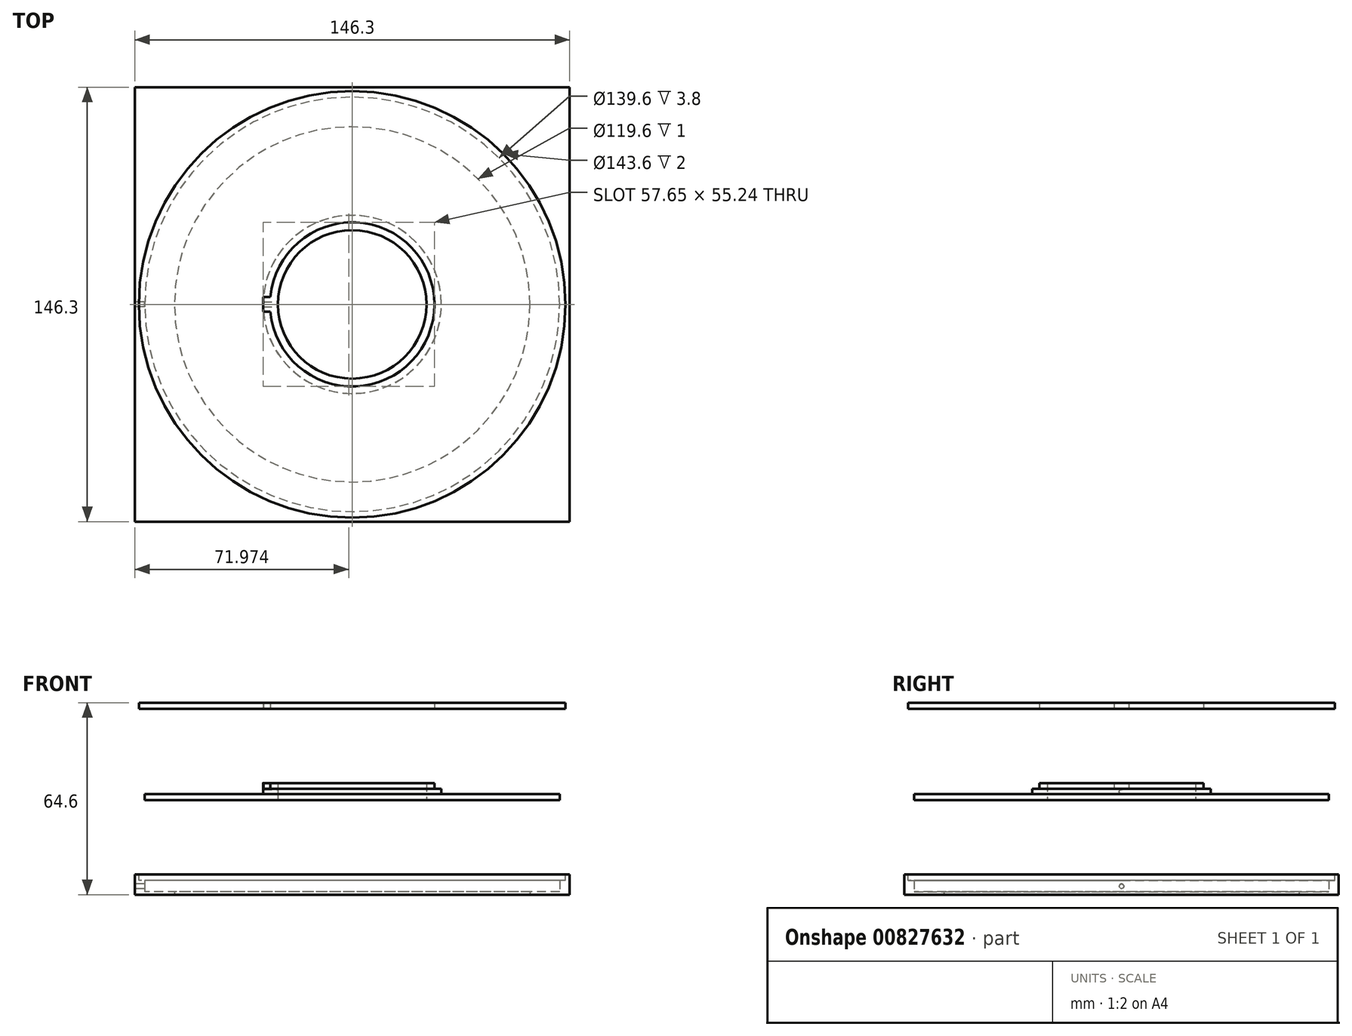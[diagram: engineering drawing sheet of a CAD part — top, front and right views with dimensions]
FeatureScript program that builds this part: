
annotation { "Feature Type Name" : "Feature", "Feature Type Description" : "" }
export const myFeature = defineFeature(function(context is Context, id is Id, definition is map)
    precondition{}
    {
        {
            var Q0;
            Q0=qCreatedBy(makeId("Top.planeOp"),FACE);
            var sketch = newSketch(context, id + "F0", { "sketchPlane" : qUnion([Q0])});
            skLineSegment(sketch, "E0.bottom", {"start": v(-73.15, 73.15) * mm, "end": v(73.15, 73.15) * mm});
            skLineSegment(sketch, "E0.top", {"start": v(-73.15, -73.15) * mm, "end": v(73.15, -73.15) * mm});
            skLineSegment(sketch, "E0.left", {"start": v(-73.15, 73.15) * mm, "end": v(-73.15, -73.15) * mm});
            skLineSegment(sketch, "E0.right", {"start": v(73.15, 73.15) * mm, "end": v(73.15, -73.15) * mm});
            skLineSegment(sketch, "E1", {"start": v(0, 73.15) * mm, "end": v(0, -73.15) * mm, "construction": true});
            skLineSegment(sketch, "E2", {"start": v(-73.15, 0) * mm, "end": v(73.15, 0) * mm, "construction": true});
            skCircle(sketch, "E3", {"center": v(0, 0) * mm, "radius": 59.8 * mm});
            skCircle(sketch, "E4", {"center": v(0, 0) * mm, "radius": 69.8 * mm});
            skCircle(sketch, "E5", {"center": v(0, 0) * mm, "radius": 25 * mm, "construction": true});
            skCircle(sketch, "E6", {"center": v(0, 0) * mm, "radius": 30 * mm, "construction": true});
            skSolve(sketch);
        }
        {
            var Q0;
            Q0=makeQuery(id+"F0.imprint","IMPRINT",FACE,{"disambiguationData":[TD([[makeQuery(id+"F0.imprint","IMPRINT",EDGE,{"derivedFrom":sQuery(id+"F0.wireOp",EDGE,"E0.bottom")}),-1.0]])]});
            extrude(context, id + "F1", {"entities" : qUnion([Q0]), "depth" : 6.8 * mm, "offsetDistance" : 25 * mm});
        }
        {
            var Q0;
            Q0=makeQuery(id+"F0.imprint","IMPRINT",FACE,{"disambiguationData":[TD([[makeQuery(id+"F0.imprint","IMPRINT",EDGE,{"derivedFrom":sQuery(id+"F0.wireOp",EDGE,"E3")}),-1.0]])]});
            extrude(context, id + "F2", {"entities" : qUnion([Q0]), "operationType" : NewBodyOperationType.ADD, "depth" : 1 * mm, "offsetDistance" : 25 * mm});
        }
        {
            var Q0;
            Q0=makeQuery(id+"F1.opExtrude","CAP_FACE",FACE,{"disambiguationData":[OSD([sQuery(id+"F0.wireOp",EDGE,"E0.bottom"),sQuery(id+"F0.wireOp",EDGE,"E0.top"),sQuery(id+"F0.wireOp",EDGE,"E0.left"),sQuery(id+"F0.wireOp",EDGE,"E0.right"),sQuery(id+"F0.wireOp",EDGE,"E4")])],"isStart":false});
            cPlane(context, id + "F3", {"entities" : qUnion([Q0]), "cplaneType" : CPlaneType.OFFSET, "offset" : 25 * mm, "width" : 150 * mm, "height" : 150 * mm});
        }
        {
            var Q0;
            Q0=qCreatedBy(id+"F3.planeOp",FACE);
            var sketch = newSketch(context, id + "F4", { "sketchPlane" : qUnion([Q0])});
            skCircle(sketch, "E7.0", {"center": v(0, 0) * mm, "radius": 25 * mm});
            skCircle(sketch, "E7.1", {"center": v(0, 0) * mm, "radius": 30 * mm});
            skCircle(sketch, "E7.2", {"center": v(0, 0) * mm, "radius": 69.8 * mm});
            skSolve(sketch);
        }
        {
            var Q0;
            Q0=makeQuery(id+"F4.imprint","IMPRINT",FACE,{"disambiguationData":[TD([[makeQuery(id+"F4.imprint","IMPRINT",EDGE,{"derivedFrom":sQuery(id+"F4.wireOp",EDGE,"E7.1")}),-1.0]])]});
            extrude(context, id + "F5", {"entities" : qUnion([Q0]), "depth" : 2 * mm, "offsetDistance" : 25 * mm});
        }
        {
            var Q0;
            Q0=makeQuery(id+"F4.imprint","IMPRINT",FACE,{"disambiguationData":[TD([[makeQuery(id+"F4.imprint","IMPRINT",EDGE,{"derivedFrom":sQuery(id+"F4.wireOp",EDGE,"E7.0")}),-1.0]])]});
            extrude(context, id + "F6", {"entities" : qUnion([Q0]), "operationType" : NewBodyOperationType.ADD, "depth" : 3.8 * mm, "offsetDistance" : 25 * mm});
        }
        {
            var Q0;
            Q0=makeQuery(id+"F6.opExtrude","CAP_FACE",FACE,{"disambiguationData":[OSD([sQuery(id+"F4.wireOp",EDGE,"E7.0"),sQuery(id+"F4.wireOp",EDGE,"E7.1")])],"isStart":false});
            var sketch = newSketch(context, id + "F7", { "sketchPlane" : qUnion([Q0])});
            skCircle(sketch, "E8", {"center": v(0, 0) * mm, "radius": 25 * mm});
            skCircle(sketch, "E9", {"center": v(0, 0) * mm, "radius": 27.65 * mm});
            skLineSegment(sketch, "E10", {"start": v(0, 0) * mm, "end": v(-30, 0) * mm, "construction": true});
            skLineSegment(sketch, "E11", {"start": v(-27.54, 2.5) * mm, "end": v(-29.9, 2.5) * mm});
            skLineSegment(sketch, "E12", {"start": v(-27.54, -2.5) * mm, "end": v(-29.9, -2.5) * mm});
            skArc(sketch, "E13", {"start": v(-29.9, 2.5) * mm, "mid": v(-30, 0) * mm, "end": v(-29.9, -2.5) * mm});
            skLineSegment(sketch, "E14", {"start": v(-28.72, 2.5) * mm, "end": v(-28.72, 0) * mm, "construction": true});
            skLineSegment(sketch, "E15", {"start": v(-28.72, 0) * mm, "end": v(-28.72, -2.5) * mm, "construction": true});
            skSolve(sketch);
        }
        {
            var Q0;
            Q0=makeQuery(id+"F7.imprint","IMPRINT",FACE,{"disambiguationData":[TD([[makeQuery(id+"F7.imprint","IMPRINT",EDGE,{"derivedFrom":sQuery(id+"F7.wireOp",EDGE,"E8")}),-1.0]])]});
            var Q1;
            {var subQ0=sQuery(id+"F7.wireOp",EDGE,"E11");Q1=makeQuery(id+"F7.imprint","IMPRINT",FACE,{"disambiguationData":[TD([[makeQuery(id+"F7.imprint","IMPRINT",EDGE,{"derivedFrom":subQ0}),1.0]])]});}
            extrude(context, id + "F8", {"entities" : qUnion([Q0, Q1]), "operationType" : NewBodyOperationType.ADD, "depth" : 2 * mm, "offsetDistance" : 25 * mm});
        }
        {
            var Q0;
            Q0=qCreatedBy(makeId("Right.planeOp"),FACE);
            var sketch = newSketch(context, id + "F9", { "sketchPlane" : qUnion([Q0])});
            skPoint(sketch, "E16.0", {"position": v(0, 35.6) * mm});
            skCircle(sketch, "E17", {"center": v(0, 34.6) * mm, "radius": 0.8 * mm});
            skSolve(sketch);
        }
        {
            var Q0;
            Q0 = qSketchRegion(id + "F9", true);
            var Q1;
            Q1=makeQuery(id+"F8.boolean.opBoolean","MERGE",FACE,{"derivedFrom":[makeQuery(id+"F6.opExtrude","SWEPT_FACE",FACE,{"disambiguationData":[OSD([sQuery(id+"F4.wireOp",EDGE,"E7.1")])]}),makeQuery(id+"F8.opExtrude","SWEPT_FACE",FACE,{"disambiguationData":[OSD([sQuery(id+"F7.wireOp",EDGE,"E13")])]})]});
            extrude(context, id + "F10", {"entities" : qUnion([Q0]), "operationType" : NewBodyOperationType.REMOVE, "endBound" : BoundingType.UP_TO_SURFACE, "oppositeDirection" : true, "depth" : 25 * mm, "endBoundEntityFace" : qUnion([Q1]), "offsetDistance" : 25 * mm});
        }
        {
            var Q0;
            Q0=makeQuery(id+"F8.opExtrude","CAP_FACE",FACE,{"disambiguationData":[OSD([sQuery(id+"F7.wireOp",EDGE,"E8"),sQuery(id+"F7.wireOp",EDGE,"E9"),sQuery(id+"F7.wireOp",EDGE,"E11"),sQuery(id+"F7.wireOp",EDGE,"E12"),sQuery(id+"F7.wireOp",EDGE,"E13")])],"isStart":false});
            cPlane(context, id + "F11", {"entities" : qUnion([Q0]), "cplaneType" : CPlaneType.OFFSET, "offset" : 25 * mm, "width" : 150 * mm, "height" : 150 * mm});
        }
        {
            var Q0;
            Q0=qCreatedBy(id+"F11.planeOp",FACE);
            var sketch = newSketch(context, id + "F12", { "sketchPlane" : qUnion([Q0])});
            skArc(sketch, "E18.0", {"start": v(-29.9, -2.5) * mm, "mid": v(30, 0) * mm, "end": v(-29.9, 2.5) * mm});
            skArc(sketch, "E18.1", {"start": v(-29.9, 2.5) * mm, "mid": v(-30, 0) * mm, "end": v(-29.9, -2.5) * mm});
            skArc(sketch, "E18.2.0", {"start": v(-27.54, -2.5) * mm, "mid": v(27.65, 0) * mm, "end": v(-27.54, 2.5) * mm});
            skLineSegment(sketch, "E18.2.1", {"start": v(-27.54, 2.5) * mm, "end": v(-29.9, 2.5) * mm});
            skArc(sketch, "E18.2.2", {"start": v(-29.9, 2.5) * mm, "mid": v(-30, 0) * mm, "end": v(-29.9, -2.5) * mm});
            skLineSegment(sketch, "E18.2.3", {"start": v(-29.9, -2.5) * mm, "end": v(-27.54, -2.5) * mm});
            skCircle(sketch, "E19.0", {"center": v(0, 0) * mm, "radius": 69.8 * mm, "construction": true});
            skCircle(sketch, "E20", {"center": v(0, 0) * mm, "radius": 71.8 * mm});
            skSolve(sketch);
        }
        {
            var Q0;
            Q0=makeQuery(id+"F12.imprint","IMPRINT",FACE,{"disambiguationData":[TD([[makeQuery(id+"F12.imprint","IMPRINT",EDGE,{"derivedFrom":sQuery(id+"F12.wireOp",EDGE,"E18.0")}),-1.0]])]});
            var Q1;
            Q1=makeQuery(id+"F12.imprint","IMPRINT",FACE,{"disambiguationData":[TD([[makeQuery(id+"F12.imprint","IMPRINT",EDGE,{"derivedFrom":sQuery(id+"F12.wireOp",EDGE,"E18.0")}),1.0]])]});
            extrude(context, id + "F13", {"entities" : qUnion([Q0, Q1]), "depth" : 2 * mm, "offsetDistance" : 25 * mm});
        }
        {
            var Q0;
            Q0=makeQuery(id+"F1.opExtrude","SWEPT_FACE",FACE,{"disambiguationData":[OSD([sQuery(id+"F0.wireOp",EDGE,"E0.left")])]});
            var sketch = newSketch(context, id + "F14", { "sketchPlane" : qUnion([Q0])});
            skLineSegment(sketch, "E21.0", {"start": v(-69.8, 1) * mm, "end": v(69.8, 1) * mm, "construction": true});
            skCircle(sketch, "E22", {"center": v(0, 2.8) * mm, "radius": 0.8 * mm});
            skPoint(sketch, "E22.centerSnap0", {"position": v(0, 1) * mm});
            skSolve(sketch);
        }
        {
            var Q0;
            Q0=makeQuery(id+"F14.imprint","IMPRINT",FACE,{"disambiguationData":[TD([[makeQuery(id+"F14.imprint","IMPRINT",EDGE,{"derivedFrom":sQuery(id+"F14.wireOp",EDGE,"E22")}),1.0]])]});
            var Q1;
            Q1 = qConstructionFilter(qBodyType(qCreatedBy(id + "F14" ,EDGE), BodyType.WIRE), ConstructionObject.NO);
            extrude(context, id + "F15", {"entities" : qUnion([Q0]), "operationType" : NewBodyOperationType.REMOVE, "surfaceEntities" : qUnion([Q1]), "endBound" : BoundingType.UP_TO_NEXT, "oppositeDirection" : true, "depth" : 25 * mm, "offsetDistance" : 25 * mm});
        }
        {
            var Q0;
            Q0=makeQuery(id+"F1.opExtrude","CAP_FACE",FACE,{"disambiguationData":[OSD([sQuery(id+"F0.wireOp",EDGE,"E0.bottom"),sQuery(id+"F0.wireOp",EDGE,"E0.top"),sQuery(id+"F0.wireOp",EDGE,"E0.left"),sQuery(id+"F0.wireOp",EDGE,"E0.right"),sQuery(id+"F0.wireOp",EDGE,"E4")])],"isStart":false});
            var sketch = newSketch(context, id + "F16", { "sketchPlane" : qUnion([Q0])});
            skCircle(sketch, "E23.0", {"center": v(0, 0) * mm, "radius": 71.8 * mm});
            skSolve(sketch);
        }
        {
            var Q0;
            Q0=makeQuery(id+"F16.imprint","IMPRINT",FACE,{"disambiguationData":[TD([[makeQuery(id+"F16.imprint","IMPRINT",EDGE,{"derivedFrom":sQuery(id+"F16.wireOp",EDGE,"E23.0")}),1.0]])]});
            extrude(context, id + "F17", {"entities" : qUnion([Q0]), "operationType" : NewBodyOperationType.REMOVE, "oppositeDirection" : true, "depth" : 2 * mm, "offsetDistance" : 25 * mm});
        }
        {
            var Q0;
            Q0=makeQuery(id+"F7.imprint","IMPRINT",FACE,{"disambiguationData":[TD([[makeQuery(id+"F7.imprint","IMPRINT",EDGE,{"derivedFrom":sQuery(id+"F7.wireOp",EDGE,"E8")}),-1.0]])]});
            var Q1;
            {var subQ0=sQuery(id+"F7.wireOp",EDGE,"E11");Q1=makeQuery(id+"F7.imprint","IMPRINT",FACE,{"disambiguationData":[TD([[makeQuery(id+"F7.imprint","IMPRINT",EDGE,{"derivedFrom":subQ0}),1.0]])]});}
            extrude(context, id + "F18", {"entities" : qUnion([Q0, Q1]), "operationType" : NewBodyOperationType.ADD, "depth" : 2 * mm, "offsetDistance" : 25 * mm});
        }
    });
